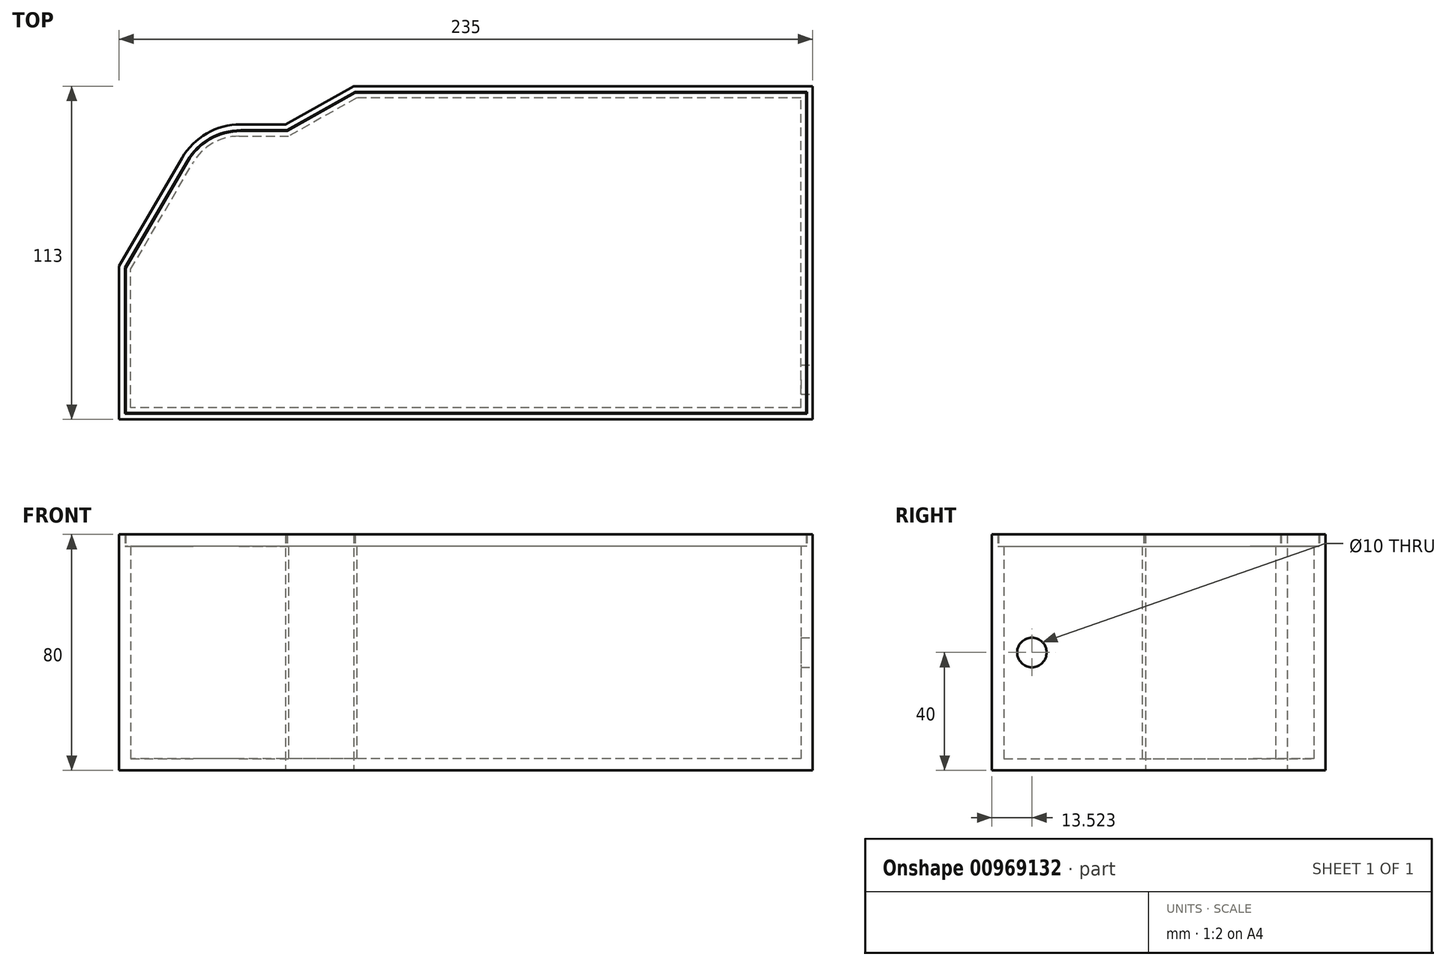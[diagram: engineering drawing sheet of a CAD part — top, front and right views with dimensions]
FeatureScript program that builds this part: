
annotation { "Feature Type Name" : "Feature", "Feature Type Description" : "" }
export const myFeature = defineFeature(function(context is Context, id is Id, definition is map)
    precondition{}
    {
        {
            var Q0;
            Q0=qCreatedBy(makeId("Top.planeOp"),FACE);
            var sketch = newSketch(context, id + "F0", { "sketchPlane" : qUnion([Q0])});
            skLineSegment(sketch, "E0", {"start": v(0, 0) * mm, "end": v(-227, 0) * mm});
            skLineSegment(sketch, "E1", {"start": v(0, 0) * mm, "end": v(0, 105) * mm});
            skLineSegment(sketch, "E2", {"start": v(-227, 0) * mm, "end": v(-227, 46.93) * mm});
            skLineSegment(sketch, "E3.0", {"start": v(0, 105) * mm, "end": v(-150.48, 105) * mm});
            skPoint(sketch, "E4.visualSharp", {"position": v(-173, 105) * mm});
            skPoint(sketch, "E5.visualSharp", {"position": v(-174.4, 109.52) * mm});
            skPoint(sketch, "E6.visualSharp", {"position": v(-227, 74.26) * mm});
            skPoint(sketch, "E7.visualSharp", {"position": v(-232.19, 77.8) * mm});
            skLineSegment(sketch, "E8", {"start": v(-227, 46.93) * mm, "end": v(-205.9, 83.1) * mm});
            skLineSegment(sketch, "E9.0", {"start": v(-294.19, -5.54) * mm, "end": v(-294.19, 47.15) * mm});
            skLineSegment(sketch, "E10.0", {"start": v(-170.19, -5.54) * mm, "end": v(-170.19, 0) * mm});
            skLineSegment(sketch, "E11", {"start": v(-190.36, 92.03) * mm, "end": v(-173.54, 92.03) * mm});
            skLineSegment(sketch, "E12.0", {"start": v(-150.48, 105) * mm, "end": v(-173.54, 92.03) * mm});
            skLineSegment(sketch, "E13.0", {"start": v(4, 109) * mm, "end": v(-151.53, 109) * mm});
            skLineSegment(sketch, "E13.1", {"start": v(4, -4) * mm, "end": v(4, 109) * mm});
            skLineSegment(sketch, "E13.2", {"start": v(-189.78, 96.03) * mm, "end": v(-174.59, 96.03) * mm});
            skLineSegment(sketch, "E13.3", {"start": v(-231, 48) * mm, "end": v(-209.65, 84.62) * mm});
            skLineSegment(sketch, "E13.4", {"start": v(-231, -4) * mm, "end": v(-231, 48) * mm});
            skLineSegment(sketch, "E13.5", {"start": v(-151.53, 109) * mm, "end": v(-174.59, 96.03) * mm});
            skLineSegment(sketch, "E13.6", {"start": v(4, -4) * mm, "end": v(-231, -4) * mm});
            skPoint(sketch, "E14.visualSharp", {"position": v(-200.7, 92.03) * mm});
            skArc(sketch, "E14.filletArc", {"start": v(-190.36, 92.03) * mm, "mid": v(-199.32, 89.64) * mm, "end": v(-205.9, 83.1) * mm});
            skPoint(sketch, "E15.visualSharp", {"position": v(-203, 96.03) * mm});
            skArc(sketch, "E15.filletArc", {"start": v(-189.78, 96.03) * mm, "mid": v(-201.24, 92.97) * mm, "end": v(-209.65, 84.62) * mm});
            skSolve(sketch);
        }
        {
            var Q0;
            Q0=qSketchRegion(id+"F0",true);
            extrude(context, id + "F1", {"entities" : qUnion([Q0]), "depth" : 72 * mm, "offsetDistance" : 25 * mm});
        }
        {
            var Q0;
            Q0=qCreatedBy(makeId("Top.planeOp"),FACE);
            var sketch = newSketch(context, id + "F2", { "sketchPlane" : qUnion([Q0])});
            skLineSegment(sketch, "E16.0", {"start": v(4, 109) * mm, "end": v(-151.53, 109) * mm});
            skLineSegment(sketch, "E17.0", {"start": v(4, -4) * mm, "end": v(4, 109) * mm});
            skLineSegment(sketch, "E18.0", {"start": v(4, -4) * mm, "end": v(-231, -4) * mm});
            skLineSegment(sketch, "E19.0", {"start": v(-231, -4) * mm, "end": v(-231, 48) * mm});
            skLineSegment(sketch, "E20.0", {"start": v(-231, 48) * mm, "end": v(-209.65, 84.62) * mm});
            skLineSegment(sketch, "E21.0", {"start": v(-189.78, 96.03) * mm, "end": v(-174.59, 96.03) * mm});
            skLineSegment(sketch, "E22.0", {"start": v(-151.53, 109) * mm, "end": v(-174.59, 96.03) * mm});
            skArc(sketch, "E23.0", {"start": v(-189.78, 96.03) * mm, "mid": v(-201.24, 92.97) * mm, "end": v(-209.65, 84.62) * mm});
            skSolve(sketch);
        }
        {
            var Q0;
            Q0=qSketchRegion(id+"F2",true);
            extrude(context, id + "F3", {"entities" : qUnion([Q0]), "operationType" : NewBodyOperationType.ADD, "oppositeDirection" : true, "depth" : 4 * mm, "offsetDistance" : 25 * mm});
        }
        {
            var Q0;
            Q0=makeQuery(id+"F1.opExtrude","CAP_FACE",FACE,{"disambiguationData":[OSD([sQuery(id+"F0.wireOp",EDGE,"E0"),sQuery(id+"F0.wireOp",EDGE,"E1"),sQuery(id+"F0.wireOp",EDGE,"E2"),sQuery(id+"F0.wireOp",EDGE,"2RP4OxQE-jADP-KTmN-HbEa-qnUMQ7Tq8s3E"),sQuery(id+"F0.wireOp",EDGE,"E3.0"),sQuery(id+"F0.wireOp",EDGE,"3fafaeca-49f5-4d3a-a4f8-4e7ef18649f5.0"),sQuery(id+"F0.wireOp",EDGE,"3fafaeca-49f5-4d3a-a4f8-4e7ef18649f5.1"),sQuery(id+"F0.wireOp",EDGE,"3fafaeca-49f5-4d3a-a4f8-4e7ef18649f5.2"),sQuery(id+"F0.wireOp",EDGE,"8a622700-e9ef-43cc-a381-9b271f172cee.0"),sQuery(id+"F0.wireOp",EDGE,"75181666-a895-4921-8e4d-bbfcd18b87d4.0"),sQuery(id+"F0.wireOp",EDGE,"gNxgNJ5l-1nvf-y9Iw-9z1v-KKdJmTJCv6Uy"),sQuery(id+"F0.wireOp",EDGE,"5jJoUbVJ-qZek-wJX6-RbB3-zVEmOnkkqNAW"),sQuery(id+"F0.wireOp",EDGE,"Vudohm3B-oAAL-XSVR-IuJz-dt4p8zKRHPaR"),sQuery(id+"F0.wireOp",EDGE,"smEqfqwM-BxS2-svOn-dxpC-lbagr5yuCO4L"),sQuery(id+"F0.wireOp",EDGE,"t7X6bI0v-Qew3-Ndkx-atJy-IQWM8BnaVnpT"),sQuery(id+"F0.wireOp",EDGE,"4lh1PQBP-lJa4-DJQ8-oKtu-ZooRv3493Byx"),sQuery(id+"F0.wireOp",EDGE,"4c8b29c2-e865-4902-8108-103171289186.trimOffspring"),sQuery(id+"F0.wireOp",EDGE,"ljndByiw-nz9o-AI8H-foGN-cbrYGZcU7gFc"),sQuery(id+"F0.wireOp",EDGE,"QAqo8eDM-adzx-s27B-teyS-FUMnTDFnUbEn"),sQuery(id+"F0.wireOp",EDGE,"0sMmZP7L-Zi46-vVs5-sRRd-WGrUDSfpJUqN"),sQuery(id+"F0.wireOp",EDGE,"E92oos4w-KrmN-Or4I-9Dvn-H4OE4QSC0Df0"),sQuery(id+"F0.wireOp",EDGE,"Zd9Vjtm7-otpH-pVzU-t58u-V2HttocbiZ7D"),sQuery(id+"F0.wireOp",EDGE,"a985586b-8bc7-496f-b6f4-b75ee5999902.trimOffspring")])],"isStart":false});
            var sketch = newSketch(context, id + "F4", { "sketchPlane" : qUnion([Q0])});
            skLineSegment(sketch, "E24.0", {"start": v(4, 109) * mm, "end": v(-151.53, 109) * mm});
            skLineSegment(sketch, "E25.0", {"start": v(4, -4) * mm, "end": v(4, 109) * mm});
            skLineSegment(sketch, "E26.0", {"start": v(4, -4) * mm, "end": v(-231, -4) * mm});
            skLineSegment(sketch, "E27.0", {"start": v(-231, -4) * mm, "end": v(-231, 48) * mm});
            skLineSegment(sketch, "E28.0", {"start": v(-231, 48) * mm, "end": v(-209.65, 84.62) * mm});
            skLineSegment(sketch, "E29.0", {"start": v(-151.53, 109) * mm, "end": v(-174.59, 96.03) * mm});
            skLineSegment(sketch, "E30.0", {"start": v(2, -2) * mm, "end": v(2, 107) * mm});
            skLineSegment(sketch, "E30.1", {"start": v(2, -2) * mm, "end": v(-229, -2) * mm});
            skLineSegment(sketch, "E30.2", {"start": v(-151, 107) * mm, "end": v(-174.06, 94.03) * mm});
            skLineSegment(sketch, "E30.5", {"start": v(2, 107) * mm, "end": v(-151, 107) * mm});
            skLineSegment(sketch, "E30.6", {"start": v(-229, -2) * mm, "end": v(-229, 47.47) * mm});
            skArc(sketch, "E31.0", {"start": v(-189.78, 96.03) * mm, "mid": v(-201.24, 92.97) * mm, "end": v(-209.65, 84.62) * mm});
            skLineSegment(sketch, "E32.0", {"start": v(-189.78, 96.03) * mm, "end": v(-174.59, 96.03) * mm});
            skLineSegment(sketch, "E33.0", {"start": v(-189.78, 94.03) * mm, "end": v(-174.06, 94.03) * mm});
            skArc(sketch, "E33.1", {"start": v(-189.78, 94.03) * mm, "mid": v(-200.24, 91.24) * mm, "end": v(-207.92, 83.6) * mm});
            skLineSegment(sketch, "E33.2", {"start": v(-229, 47.47) * mm, "end": v(-207.92, 83.6) * mm});
            skSolve(sketch);
        }
        {
            var Q0;
            Q0=makeQuery(id+"F4.imprint","IMPRINT",FACE,{"disambiguationData":[TD([[makeQuery(id+"F4.imprint","IMPRINT",EDGE,{"derivedFrom":sQuery(id+"F4.wireOp",EDGE,"E24.0")}),1.0]])]});
            extrude(context, id + "F5", {"entities" : qUnion([Q0]), "operationType" : NewBodyOperationType.ADD, "depth" : 4 * mm, "offsetDistance" : 25 * mm});
        }
        {
            var Q0;
            Q0=makeQuery(id+"F5.boolean.opBoolean","MERGE",FACE,{"derivedFrom":[makeQuery(id+"F3.boolean.opBoolean","MERGE",FACE,{"derivedFrom":[makeQuery(id+"F1.opExtrude","SWEPT_FACE",FACE,{"disambiguationData":[OSD([sQuery(id+"F0.wireOp",EDGE,"E13.1")])]}),makeQuery(id+"F3.opExtrude","SWEPT_FACE",FACE,{"disambiguationData":[OSD([sQuery(id+"F2.wireOp",EDGE,"E17.0")])]})]}),makeQuery(id+"F5.opExtrude","SWEPT_FACE",FACE,{"disambiguationData":[OSD([sQuery(id+"F4.wireOp",EDGE,"E25.0")])]})]});
            var sketch = newSketch(context, id + "F6", { "sketchPlane" : qUnion([Q0])});
            skLineSegment(sketch, "E34.0.0", {"start": v(0, 0) * mm, "end": v(0, 0) * mm});
            skLineSegment(sketch, "E34.0.1", {"start": v(0, 0) * mm, "end": v(0, 72) * mm});
            skLineSegment(sketch, "E34.0.2", {"start": v(0, 72) * mm, "end": v(0, 72) * mm});
            skLineSegment(sketch, "E34.0.3", {"start": v(0, 0) * mm, "end": v(0, 72) * mm});
            skLineSegment(sketch, "E35", {"start": v(0, 36) * mm, "end": v(0, 36) * mm});
            skCircle(sketch, "E36", {"center": v(9.52, 36) * mm, "radius": 5 * mm});
            skSolve(sketch);
        }
        {
            var Q0;
            Q0=makeQuery(id+"F6.imprint","IMPRINT",FACE,{"disambiguationData":[TD([[makeQuery(id+"F6.imprint","IMPRINT",EDGE,{"derivedFrom":sQuery(id+"F6.wireOp",EDGE,"E36")}),1.0]])]});
            extrude(context, id + "F7", {"entities" : qUnion([Q0]), "operationType" : NewBodyOperationType.REMOVE, "oppositeDirection" : true, "depth" : 25 * mm, "offsetDistance" : 25 * mm});
        }
        {
            var Q0;
            Q0=makeQuery(id+"F1.opExtrude","CAP_FACE",FACE,{"disambiguationData":[OSD([sQuery(id+"F0.wireOp",EDGE,"E0"),sQuery(id+"F0.wireOp",EDGE,"E1"),sQuery(id+"F0.wireOp",EDGE,"E2"),sQuery(id+"F0.wireOp",EDGE,"E3.0"),sQuery(id+"F0.wireOp",EDGE,"E8"),sQuery(id+"F0.wireOp",EDGE,"E11"),sQuery(id+"F0.wireOp",EDGE,"E12.0"),sQuery(id+"F0.wireOp",EDGE,"E13.0"),sQuery(id+"F0.wireOp",EDGE,"E13.1"),sQuery(id+"F0.wireOp",EDGE,"E13.2"),sQuery(id+"F0.wireOp",EDGE,"E13.3"),sQuery(id+"F0.wireOp",EDGE,"E13.4"),sQuery(id+"F0.wireOp",EDGE,"E13.5"),sQuery(id+"F0.wireOp",EDGE,"E13.6"),sQuery(id+"F0.wireOp",EDGE,"E14.filletArc"),sQuery(id+"F0.wireOp",EDGE,"E15.filletArc")])],"isStart":false});
            var sketch = newSketch(context, id + "F8", { "sketchPlane" : qUnion([Q0])});
            skArc(sketch, "E37.0", {"start": v(-189.78, 94.03) * mm, "mid": v(-200.24, 91.24) * mm, "end": v(-207.92, 83.6) * mm});
            skLineSegment(sketch, "E38.0", {"start": v(-189.78, 94.03) * mm, "end": v(-174.06, 94.03) * mm});
            skLineSegment(sketch, "E39.0", {"start": v(-151, 107) * mm, "end": v(-174.06, 94.03) * mm});
            skLineSegment(sketch, "E40.0", {"start": v(2, 107) * mm, "end": v(-151, 107) * mm});
            skLineSegment(sketch, "E41.0", {"start": v(-229, 47.47) * mm, "end": v(-207.92, 83.6) * mm});
            skLineSegment(sketch, "E42.0", {"start": v(-229, -2) * mm, "end": v(-229, 47.47) * mm});
            skLineSegment(sketch, "E43.0", {"start": v(2, -2) * mm, "end": v(-229, -2) * mm});
            skLineSegment(sketch, "E44.0", {"start": v(2, -2) * mm, "end": v(2, 107) * mm});
            skArc(sketch, "E45.0", {"start": v(-189.78, 93.78) * mm, "mid": v(-200.12, 91.02) * mm, "end": v(-207.7, 83.48) * mm});
            skLineSegment(sketch, "E45.1", {"start": v(-228.75, 47.4) * mm, "end": v(-207.7, 83.48) * mm});
            skLineSegment(sketch, "E45.2", {"start": v(-189.78, 93.78) * mm, "end": v(-174, 93.78) * mm});
            skLineSegment(sketch, "E45.3", {"start": v(-228.75, -1.75) * mm, "end": v(-228.75, 47.4) * mm});
            skLineSegment(sketch, "E45.4", {"start": v(-150.94, 106.75) * mm, "end": v(-174, 93.78) * mm});
            skLineSegment(sketch, "E45.5", {"start": v(1.75, 106.75) * mm, "end": v(-150.94, 106.75) * mm});
            skLineSegment(sketch, "E45.6", {"start": v(1.75, -1.75) * mm, "end": v(1.75, 106.75) * mm});
            skLineSegment(sketch, "E45.7", {"start": v(1.75, -1.75) * mm, "end": v(-228.75, -1.75) * mm});
            skSolve(sketch);
        }
        {
            var Q0;
            Q0=makeQuery(id+"F8.imprint","IMPRINT",FACE,{"disambiguationData":[TD([[makeQuery(id+"F8.imprint","IMPRINT",EDGE,{"derivedFrom":makeQuery(id+"F1.opExtrude","CAP_EDGE",EDGE,{"disambiguationData":[OSD([sQuery(id+"F0.wireOp",EDGE,"E0")])],"isStart":false})}),-1.0]])]});
            var Q1;
            Q1=makeQuery(id+"F8.imprint","IMPRINT",FACE,{"disambiguationData":[TD([[makeQuery(id+"F8.imprint","IMPRINT",EDGE,{"derivedFrom":sQuery(id+"F8.wireOp",EDGE,"E45.0")}),1.0]])]});
            extrude(context, id + "F9", {"entities" : qUnion([Q0, Q1]), "depth" : 4 * mm, "offsetDistance" : 25 * mm});
        }
    });
